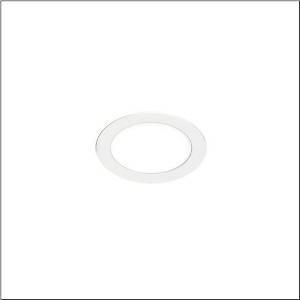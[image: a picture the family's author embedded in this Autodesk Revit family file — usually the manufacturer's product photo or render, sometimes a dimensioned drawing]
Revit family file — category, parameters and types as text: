
# Revit family: lunis_41_flat_51dr107dgba
name_source: partatom
category: Lighting Fixtures
units: mm (PartAtom-declared; Revit-internal decimal feet)

## family parameters
Cut with Voids When Loaded = No
Host = Face
Light Source = No
Part Type = Normal
Room Calculation Point = No
Round Connector Dimension = Use Diameter
Shared = No

## types (1)
- --- (1 x LED, 1360 lm, 15 W, 4000K)
    Apparent Load = 15 VA
    CIE Flux Codes = 49 80 96 100 100
    Color Rendering = 80
    Color Temperature = 4000K
    Default Elevation = 1800 mm
    Description = Lunis 41 Flat, downlight, light emission: direct distribution, LED rated luminous flux: 1.250lm, light colour: 830/840, control gear: ECG, mains connection: 230V, AC, 50/60Hz, housing, round, of aluminium, coated, traffic white (RAL 9016), diameter: 170mm, protection rating (complete): IP20, protection rating (on room side): IP44, insulation class (complete): insulation class II (safety insulation), certification: CE, permissible ambient temperature for indoor applications: -20..+40°C, packaging unit: 1 piece
    Height = 0 mm  [stored 0 ft]
    Lamp = 1 x LED
    Lamp Light Flux = 1360 lm
    Lamp Power = 15 W
    Lamp count = 1
    Length = 170 mm  [stored 0.557743 ft]
    Luminous efficacy = 91 lm/W
    Manufacturer = Siteco
    ModVariant = No
    Model = 51DR107DGBA
    Mounting Place = Ceiling
    Mounting Type = Recessed
    Number of Poles = 1
    OnlyDefault = Yes
    Power Factor = 1
    Product Name = Lunis 41 Flat
    Product group = downlight
    ProductGroupID = 401
    Protection Class = Protection class II
    Protection Degree = IP 20
    RLX_Detail_Level = 1
    RLX_Emergency_Light_Flux = 0 lm
    RLX_Emergency_Type = 0
    RLX_Emergency_Type_DB = No
    RlxData = <blob elided: 24229 chars, md5=369911a7>
    Socket = socket
    Standby Power = 0 W
    System Light Flux = 1360 lm
    System Power = 15 W
    Type Comments = factory setting: colour temperature 4000K
    Type Image = l_1340921.jpg
    URL = http://relux.com
    VarID = @adj_193037
    Voltage = 0 V
    Weight = 0.00 kg
    Width = 0 mm  [stored 0 ft]

note: [stored X ft] marks values corroborated as IEEE doubles in the binary element streams (Revit-internal decimal feet)

## geometry (parser evidence)
native form markers: Blend x4, Sweep x10
no freeform markers — native parametric forms only
